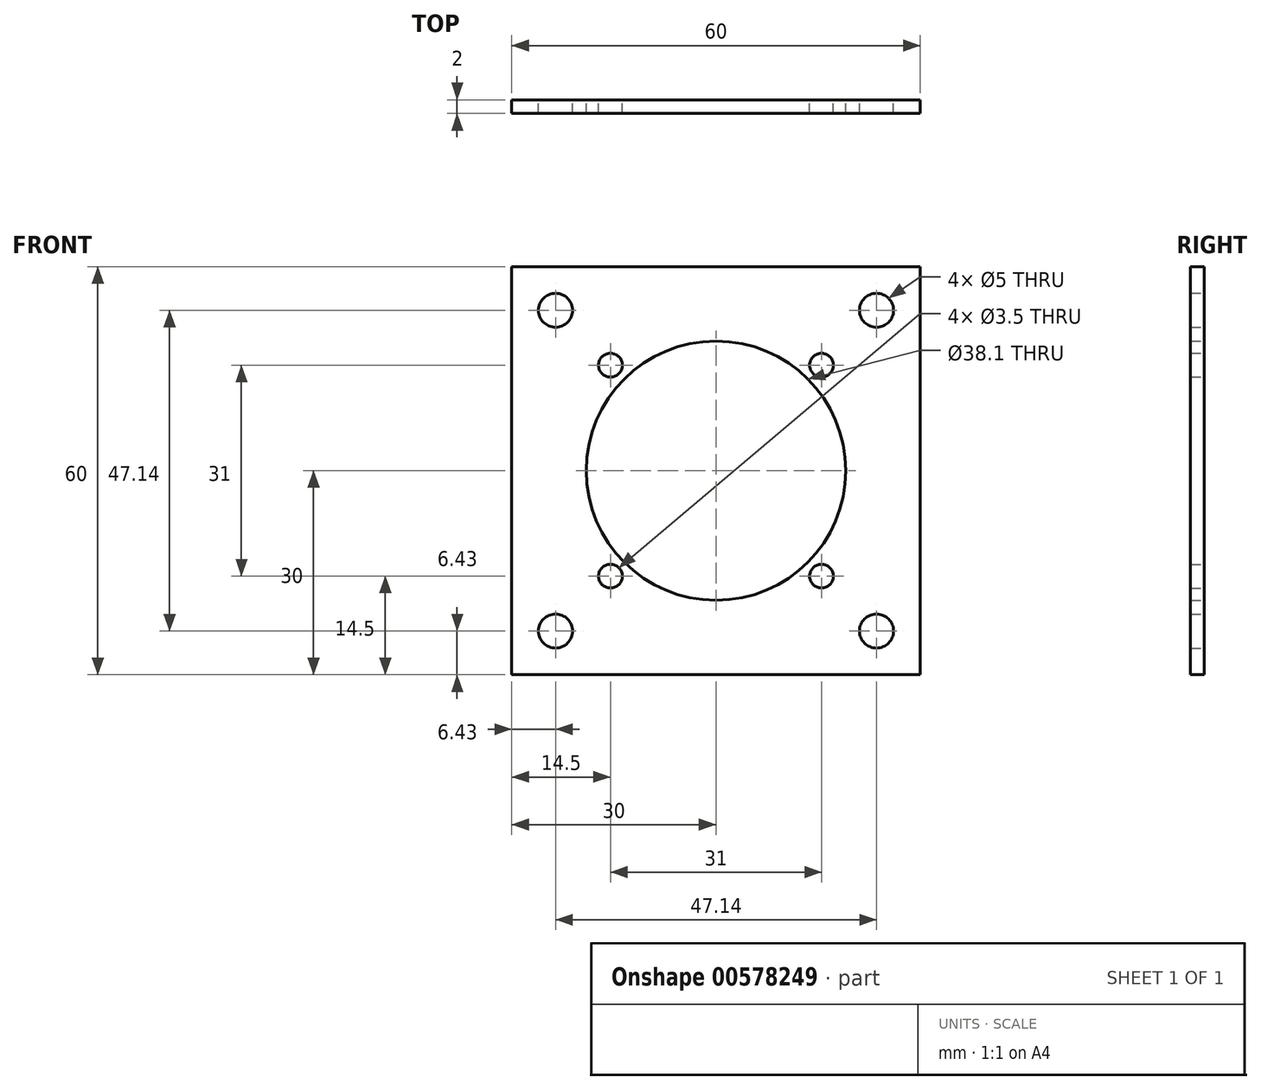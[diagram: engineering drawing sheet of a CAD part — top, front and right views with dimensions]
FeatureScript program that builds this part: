
annotation { "Feature Type Name" : "Feature", "Feature Type Description" : "" }
export const myFeature = defineFeature(function(context is Context, id is Id, definition is map)
    precondition{}
    {
        {
            var Q0;
            Q0=qCreatedBy(makeId("Front.planeOp"),FACE);
            var sketch = newSketch(context, id + "F0", { "sketchPlane" : qUnion([Q0])});
            skCircle(sketch, "E0", {"center": v(0, 0) * mm, "radius": 19.05 * mm});
            skCircle(sketch, "E1", {"center": v(23.57, 23.57) * mm, "radius": 2.5 * mm});
            skCircle(sketch, "E2.MirrorC", {"center": v(-23.57, 23.57) * mm, "radius": 2.5 * mm});
            skCircle(sketch, "E3.MirrorC", {"center": v(-23.57, -23.57) * mm, "radius": 2.5 * mm});
            skCircle(sketch, "E4.MirrorC", {"center": v(23.57, -23.57) * mm, "radius": 2.5 * mm});
            skCircle(sketch, "E5", {"center": v(15.5, 15.5) * mm, "radius": 1.75 * mm});
            skCircle(sketch, "E6.MirrorC", {"center": v(-15.5, 15.5) * mm, "radius": 1.75 * mm});
            skCircle(sketch, "E7.MirrorC", {"center": v(-15.5, -15.5) * mm, "radius": 1.75 * mm});
            skCircle(sketch, "E8.MirrorC", {"center": v(15.5, -15.5) * mm, "radius": 1.75 * mm});
            skLineSegment(sketch, "E9.bottom", {"start": v(-30, 30) * mm, "end": v(30, 30) * mm});
            skLineSegment(sketch, "E9.top", {"start": v(-30, -30) * mm, "end": v(30, -30) * mm});
            skLineSegment(sketch, "E9.left", {"start": v(-30, 30) * mm, "end": v(-30, -30) * mm});
            skLineSegment(sketch, "E9.right", {"start": v(30, 30) * mm, "end": v(30, -30) * mm});
            skSolve(sketch);
        }
        {
            var Q0;
            Q0=makeQuery(id+"F0.imprint","IMPRINT",FACE,{"disambiguationData":[TD([[makeQuery(id+"F0.imprint","IMPRINT",EDGE,{"derivedFrom":sQuery(id+"F0.wireOp",EDGE,"E0")}),-1.0]])]});
            extrude(context, id + "F1", {"entities" : qUnion([Q0]), "depth" : 2 * mm, "offsetDistance" : 25 * mm});
        }
    });
